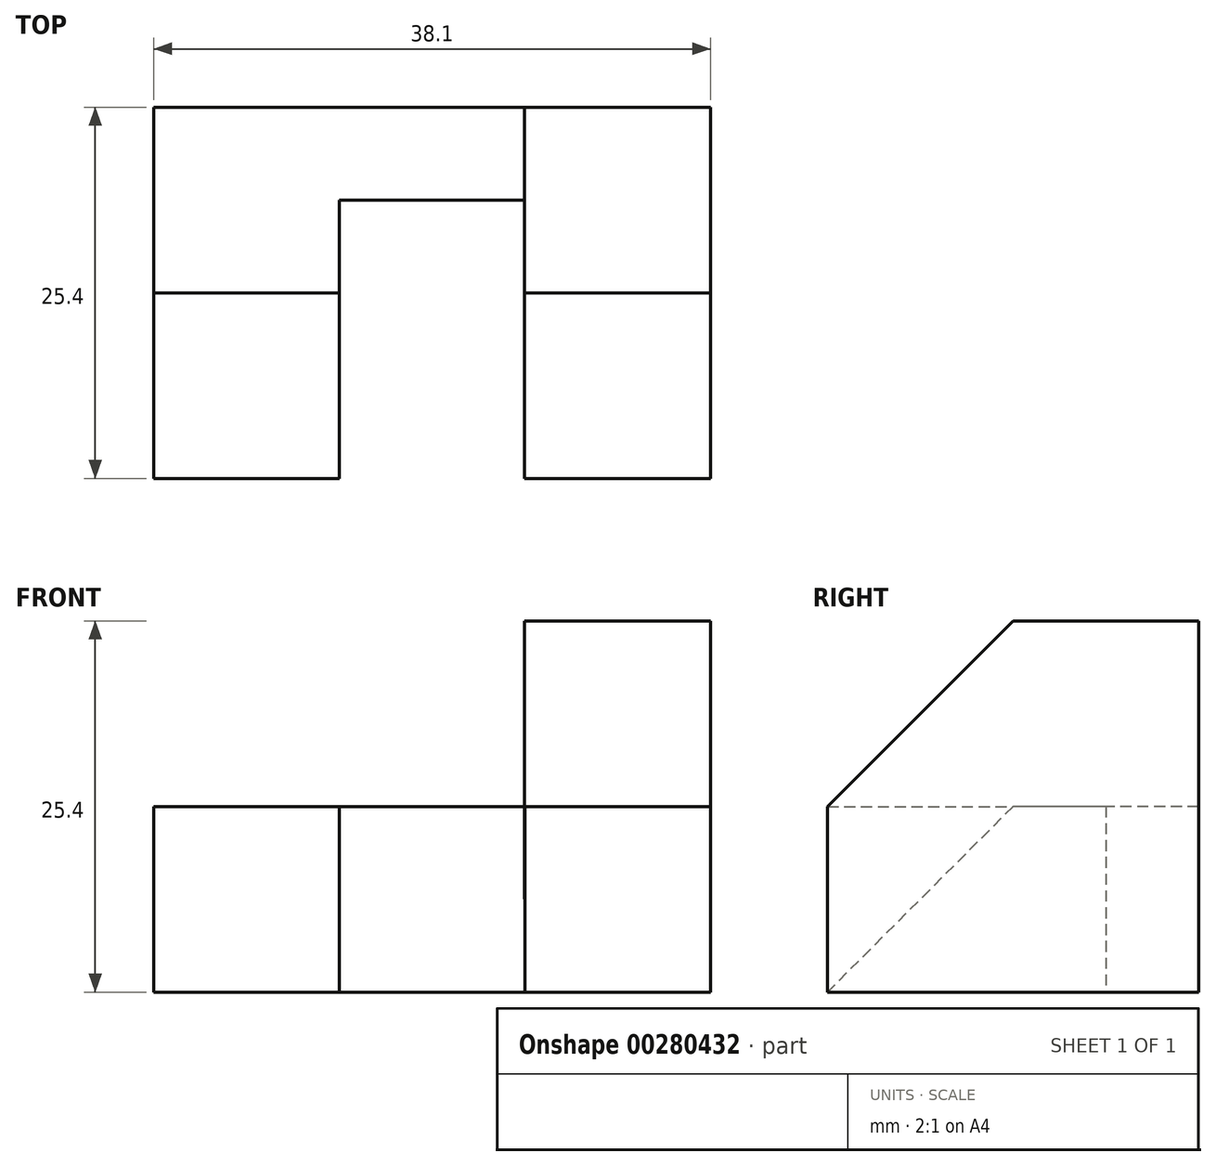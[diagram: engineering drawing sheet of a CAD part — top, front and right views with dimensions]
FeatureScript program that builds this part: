
annotation { "Feature Type Name" : "Feature", "Feature Type Description" : "" }
export const myFeature = defineFeature(function(context is Context, id is Id, definition is map)
    precondition{}
    {
        {
            var Q0;
            Q0=qCreatedBy(makeId("Front.planeOp"),FACE);
            var sketch = newSketch(context, id + "F0", { "sketchPlane" : qUnion([Q0])});
            skLineSegment(sketch, "E0", {"start": v(0, 0) * mm, "end": v(38.1, 0) * mm});
            skLineSegment(sketch, "E1", {"start": v(38.1, 0) * mm, "end": v(38.1, 25.4) * mm});
            skLineSegment(sketch, "E2", {"start": v(38.1, 25.4) * mm, "end": v(0, 25.4) * mm});
            skLineSegment(sketch, "E3", {"start": v(0, 25.4) * mm, "end": v(0, 0) * mm});
            skSolve(sketch);
        }
        {
            var Q0;
            Q0=qSketchRegion(id+"F0",true);
            extrude(context, id + "F1", {"entities" : qUnion([Q0]), "endBound" : BoundingType.SYMMETRIC, "depth" : 25.4 * mm});
        }
        {
            var Q0;
            Q0=makeQuery(id+"F1.opExtrude","CAP_FACE",FACE,{"disambiguationData":[OSD([sQuery(id+"F0.wireOp",EDGE,"E0"),sQuery(id+"F0.wireOp",EDGE,"E1"),sQuery(id+"F0.wireOp",EDGE,"E2"),sQuery(id+"F0.wireOp",EDGE,"E3")])],"isStart":false});
            var sketch = newSketch(context, id + "F2", { "sketchPlane" : qUnion([Q0])});
            skLineSegment(sketch, "E4", {"start": v(0, 25.4) * mm, "end": v(12.7, 25.4) * mm});
            skLineSegment(sketch, "E5", {"start": v(12.7, 25.4) * mm, "end": v(25.36, 25.4) * mm});
            skLineSegment(sketch, "E6", {"start": v(25.36, 25.4) * mm, "end": v(38.1, 25.4) * mm});
            skLineSegment(sketch, "E7", {"start": v(12.7, 25.4) * mm, "end": v(12.7, 12.7) * mm});
            skLineSegment(sketch, "E8", {"start": v(12.7, 12.7) * mm, "end": v(25.36, 12.7) * mm});
            skLineSegment(sketch, "E9", {"start": v(25.36, 12.7) * mm, "end": v(25.36, 25.4) * mm});
            skLineSegment(sketch, "E10", {"start": v(12.7, 12.7) * mm, "end": v(12.7, 0) * mm});
            skLineSegment(sketch, "E11", {"start": v(12.7, 0) * mm, "end": v(25.4, 0) * mm});
            skLineSegment(sketch, "E12", {"start": v(25.4, 0) * mm, "end": v(25.36, 12.7) * mm});
            skLineSegment(sketch, "E13", {"start": v(12.7, 12.7) * mm, "end": v(0, 12.7) * mm});
            skLineSegment(sketch, "E14", {"start": v(0, 12.7) * mm, "end": v(0, 25.4) * mm});
            skLineSegment(sketch, "E15", {"start": v(12.7, 25.4) * mm, "end": v(0, 25.4) * mm});
            skSolve(sketch);
        }
        {
            var Q0;
            Q0=makeQuery(id+"F2.imprint","IMPRINT",FACE,{"disambiguationData":[TD([[makeQuery(id+"F2.imprint","IMPRINT",EDGE,{"derivedFrom":sQuery(id+"F2.wireOp",EDGE,"E8")}),-1.0]])]});
            extrude(context, id + "F3", {"entities" : qUnion([Q0]), "operationType" : NewBodyOperationType.REMOVE, "oppositeDirection" : true, "depth" : 19.05 * mm});
        }
        {
            var Q0;
            Q0=makeQuery(id+"F2.imprint","IMPRINT",FACE,{"disambiguationData":[TD([[makeQuery(id+"F2.imprint","IMPRINT",EDGE,{"derivedFrom":sQuery(id+"F2.wireOp",EDGE,"E5")}),1.0]])]});
            var Q1;
            Q1=makeQuery(id+"F2.imprint","IMPRINT",FACE,{"disambiguationData":[TD([[makeQuery(id+"F2.imprint","IMPRINT",EDGE,{"derivedFrom":sQuery(id+"F2.wireOp",EDGE,"E7")}),-1.0]])]});
            extrude(context, id + "F4", {"entities" : qUnion([Q0, Q1]), "operationType" : NewBodyOperationType.REMOVE, "endBound" : BoundingType.THROUGH_ALL, "oppositeDirection" : true, "depth" : 25.4 * mm});
        }
        {
            var Q0;
            Q0=makeQuery(id+"F1.opExtrude","SWEPT_FACE",FACE,{"disambiguationData":[OSD([sQuery(id+"F0.wireOp",EDGE,"E3")])]});
            var sketch = newSketch(context, id + "F5", { "sketchPlane" : qUnion([Q0])});
            skLineSegment(sketch, "E16", {"start": v(0, 12.7) * mm, "end": v(12.7, 0) * mm});
            skLineSegment(sketch, "E17", {"start": v(12.7, 0) * mm, "end": v(12.7, 12.7) * mm});
            skLineSegment(sketch, "E18", {"start": v(12.7, 12.7) * mm, "end": v(0, 12.7) * mm});
            skSolve(sketch);
        }
        {
            var Q0;
            Q0=makeQuery(id+"F5.imprint","IMPRINT",FACE,{"disambiguationData":[TD([[makeQuery(id+"F5.imprint","IMPRINT",EDGE,{"derivedFrom":sQuery(id+"F5.wireOp",EDGE,"E16")}),1.0]])]});
            extrude(context, id + "F6", {"entities" : qUnion([Q0]), "operationType" : NewBodyOperationType.REMOVE, "oppositeDirection" : true, "depth" : 25.4 * mm});
        }
        {
            var Q0;
            Q0=makeQuery(id+"F1.opExtrude","SWEPT_FACE",FACE,{"disambiguationData":[OSD([sQuery(id+"F0.wireOp",EDGE,"E1")])]});
            var sketch = newSketch(context, id + "F7", { "sketchPlane" : qUnion([Q0])});
            skLineSegment(sketch, "E19", {"start": v(0, 25.4) * mm, "end": v(-12.7, 12.7) * mm});
            skLineSegment(sketch, "E20", {"start": v(-12.7, 12.7) * mm, "end": v(-12.7, 25.4) * mm});
            skLineSegment(sketch, "E21", {"start": v(-12.7, 25.4) * mm, "end": v(0, 25.4) * mm});
            skSolve(sketch);
        }
        {
            var Q0;
            Q0=makeQuery(id+"F7.imprint","IMPRINT",FACE,{"disambiguationData":[TD([[makeQuery(id+"F7.imprint","IMPRINT",EDGE,{"derivedFrom":sQuery(id+"F7.wireOp",EDGE,"E19")}),-1.0]])]});
            extrude(context, id + "F8", {"entities" : qUnion([Q0]), "operationType" : NewBodyOperationType.REMOVE, "endBound" : BoundingType.THROUGH_ALL, "oppositeDirection" : true, "depth" : 25.4 * mm});
        }
    });
